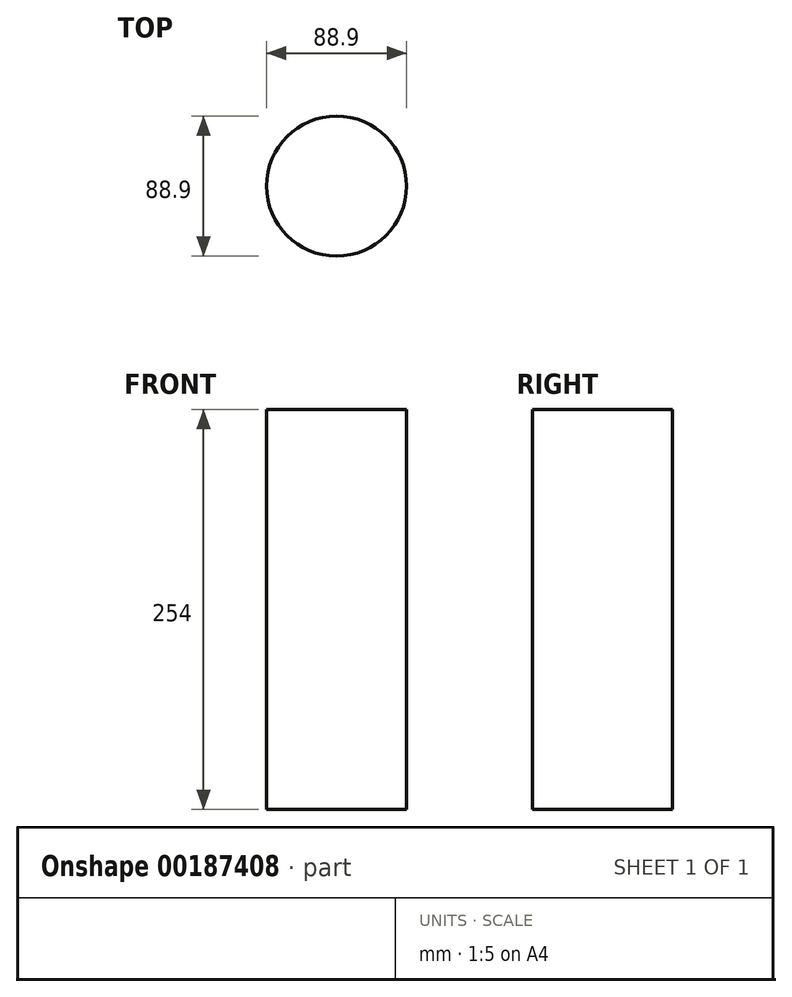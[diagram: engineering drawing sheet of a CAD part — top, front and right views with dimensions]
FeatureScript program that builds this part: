
annotation { "Feature Type Name" : "Feature", "Feature Type Description" : "" }
export const myFeature = defineFeature(function(context is Context, id is Id, definition is map)
    precondition{}
    {
        {
            var Q0;
            Q0=qCreatedBy(makeId("Top.planeOp"),FACE);
            var sketch = newSketch(context, id + "F0", { "sketchPlane" : qUnion([Q0])});
            skCircle(sketch, "E0", {"center": v(0, 0) * mm, "radius": 44.45 * mm});
            skSolve(sketch);
        }
        {
            var Q0;
            Q0=makeQuery(id+"F0.imprint","IMPRINT",FACE,{"disambiguationData":[TD([[makeQuery(id+"F0.imprint","IMPRINT",EDGE,{"derivedFrom":sQuery(id+"F0.wireOp",EDGE,"E0")}),1.0]])]});
            extrude(context, id + "F1", {"entities" : qUnion([Q0]), "depth" : 254 * mm});
        }
    });
